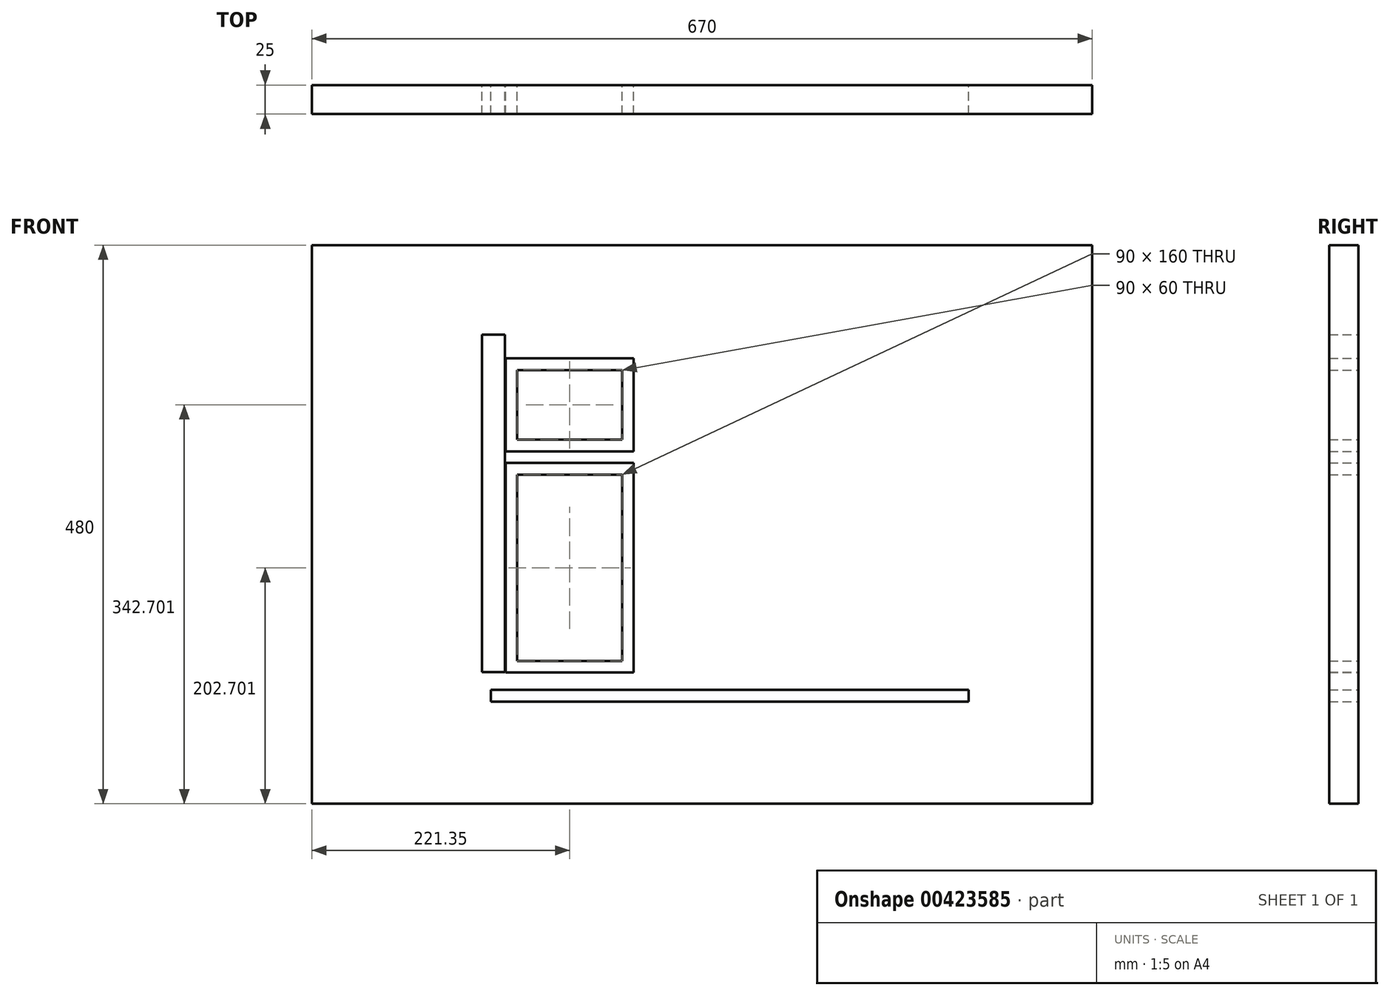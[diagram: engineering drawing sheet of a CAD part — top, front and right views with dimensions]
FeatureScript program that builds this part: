
annotation { "Feature Type Name" : "Feature", "Feature Type Description" : "" }
export const myFeature = defineFeature(function(context is Context, id is Id, definition is map)
    precondition{}
    {
        {
            var Q0;
            Q0=qCreatedBy(makeId("Front.planeOp"),FACE);
            var sketch = newSketch(context, id + "F0", { "sketchPlane" : qUnion([Q0])});
            skLineSegment(sketch, "E0.bottom", {"start": v(-49.7, 42.78) * mm, "end": v(40.3, 42.78) * mm});
            skLineSegment(sketch, "E0.top", {"start": v(-49.7, -17.22) * mm, "end": v(40.3, -17.22) * mm});
            skLineSegment(sketch, "E0.left", {"start": v(-49.7, 42.78) * mm, "end": v(-49.7, -17.22) * mm});
            skLineSegment(sketch, "E0.right", {"start": v(40.3, 42.78) * mm, "end": v(40.3, -17.22) * mm});
            skLineSegment(sketch, "E1.bottom", {"start": v(-59.7, 52.78) * mm, "end": v(50.3, 52.78) * mm});
            skLineSegment(sketch, "E1.top", {"start": v(-59.7, -27.22) * mm, "end": v(50.3, -27.22) * mm});
            skLineSegment(sketch, "E1.left", {"start": v(-59.7, 52.78) * mm, "end": v(-59.7, -27.22) * mm});
            skLineSegment(sketch, "E1.right", {"start": v(50.3, 52.78) * mm, "end": v(50.3, -27.22) * mm});
            skLineSegment(sketch, "E2", {"start": v(-49.7, 12.78) * mm, "end": v(-59.7, 12.78) * mm, "construction": true});
            skLineSegment(sketch, "E3", {"start": v(40.3, 12.78) * mm, "end": v(50.3, 12.78) * mm, "construction": true});
            skLineSegment(sketch, "E4.bottom", {"start": v(-55, 0) * mm, "end": v(55, 0) * mm});
            skLineSegment(sketch, "E5.bottom", {"start": v(-59.7, -37.22) * mm, "end": v(50.3, -37.22) * mm});
            skLineSegment(sketch, "E5.top", {"start": v(-59.7, -217.22) * mm, "end": v(50.3, -217.22) * mm});
            skLineSegment(sketch, "E5.left", {"start": v(-59.7, -37.22) * mm, "end": v(-59.7, -217.22) * mm});
            skLineSegment(sketch, "E5.right", {"start": v(50.3, -37.22) * mm, "end": v(50.3, -217.22) * mm});
            skLineSegment(sketch, "E6", {"start": v(-59.7, -27.22) * mm, "end": v(-59.7, -37.22) * mm, "construction": true});
            skLineSegment(sketch, "E7.bottom", {"start": v(-49.7, -47.22) * mm, "end": v(40.3, -47.22) * mm});
            skLineSegment(sketch, "E7.top", {"start": v(-49.7, -207.22) * mm, "end": v(40.3, -207.22) * mm});
            skLineSegment(sketch, "E7.left", {"start": v(-49.7, -47.22) * mm, "end": v(-49.7, -207.22) * mm});
            skLineSegment(sketch, "E7.right", {"start": v(40.3, -47.22) * mm, "end": v(40.3, -207.22) * mm});
            skLineSegment(sketch, "E8", {"start": v(40.3, -127.22) * mm, "end": v(50.3, -127.22) * mm, "construction": true});
            skLineSegment(sketch, "E9", {"start": v(-59.7, -127.22) * mm, "end": v(-49.7, -127.22) * mm, "construction": true});
            skSolve(sketch);
        }
        {
            var Q0;
            Q0 = qSketchRegion(id + "F0", true);
            extrude(context, id + "F1", {"entities" : qUnion([Q0]), "depth" : 25 * mm, "offsetDistance" : 25 * mm});
        }
        {
            var Q0;
            Q0=qCreatedBy(makeId("Front.planeOp"),FACE);
            var sketch = newSketch(context, id + "F2", { "sketchPlane" : qUnion([Q0])});
            skLineSegment(sketch, "E10.bottom", {"start": v(-80.15, 73.08) * mm, "end": v(-60.15, 73.08) * mm});
            skLineSegment(sketch, "E10.top", {"start": v(-80.15, -216.92) * mm, "end": v(-60.15, -216.92) * mm});
            skLineSegment(sketch, "E10.left", {"start": v(-80.15, 73.08) * mm, "end": v(-80.15, -216.92) * mm});
            skLineSegment(sketch, "E10.right", {"start": v(-60.15, 73.08) * mm, "end": v(-60.15, -216.92) * mm});
            skSolve(sketch);
        }
        {
            var Q0;
            Q0=qCreatedBy(makeId("Front.planeOp"),FACE);
            var sketch = newSketch(context, id + "F3", { "sketchPlane" : qUnion([Q0])});
            skLineSegment(sketch, "E11.bottom", {"start": v(-72.23, -232.12) * mm, "end": v(337.77, -232.12) * mm});
            skLineSegment(sketch, "E11.top", {"start": v(-72.23, -242.12) * mm, "end": v(337.77, -242.12) * mm});
            skLineSegment(sketch, "E11.left", {"start": v(-72.23, -232.12) * mm, "end": v(-72.23, -242.12) * mm});
            skLineSegment(sketch, "E11.right", {"start": v(337.77, -232.12) * mm, "end": v(337.77, -242.12) * mm});
            skSolve(sketch);
        }
        {
            var Q0;
            Q0=makeQuery(id+"F2.imprint","IMPRINT",FACE,{"disambiguationData":[TD([[makeQuery(id+"F2.imprint","IMPRINT",EDGE,{"derivedFrom":sQuery(id+"F2.wireOp",EDGE,"E10.bottom")}),-1.0]])]});
            extrude(context, id + "F4", {"entities" : qUnion([Q0]), "depth" : 25 * mm, "offsetDistance" : 25 * mm});
        }
        {
            var Q0;
            Q0=makeQuery(id+"F3.imprint","IMPRINT",FACE,{"disambiguationData":[TD([[makeQuery(id+"F3.imprint","IMPRINT",EDGE,{"derivedFrom":sQuery(id+"F3.wireOp",EDGE,"E11.bottom")}),-1.0]])]});
            extrude(context, id + "F5", {"entities" : qUnion([Q0]), "depth" : 25 * mm, "offsetDistance" : 25 * mm});
        }
        {
            var Q0;
            Q0=qCreatedBy(makeId("Front.planeOp"),FACE);
            var sketch = newSketch(context, id + "F6", { "sketchPlane" : qUnion([Q0])});
            skLineSegment(sketch, "E12.bottom", {"start": v(-226.06, 150.08) * mm, "end": v(443.94, 150.08) * mm});
            skLineSegment(sketch, "E12.top", {"start": v(-226.06, -329.92) * mm, "end": v(443.94, -329.92) * mm});
            skLineSegment(sketch, "E12.left", {"start": v(-226.06, 150.08) * mm, "end": v(-226.06, -329.92) * mm});
            skLineSegment(sketch, "E12.right", {"start": v(443.94, 150.08) * mm, "end": v(443.94, -329.92) * mm});
            skSolve(sketch);
        }
        {
            var Q0;
            Q0=makeQuery(id+"F6.imprint","IMPRINT",FACE,{"disambiguationData":[TD([[makeQuery(id+"F6.imprint","IMPRINT",EDGE,{"derivedFrom":sQuery(id+"F6.wireOp",EDGE,"E12.bottom")}),-1.0]])]});
            extrude(context, id + "F7", {"entities" : qUnion([Q0]), "depth" : 25 * mm, "offsetDistance" : 25 * mm});
        }
    });
